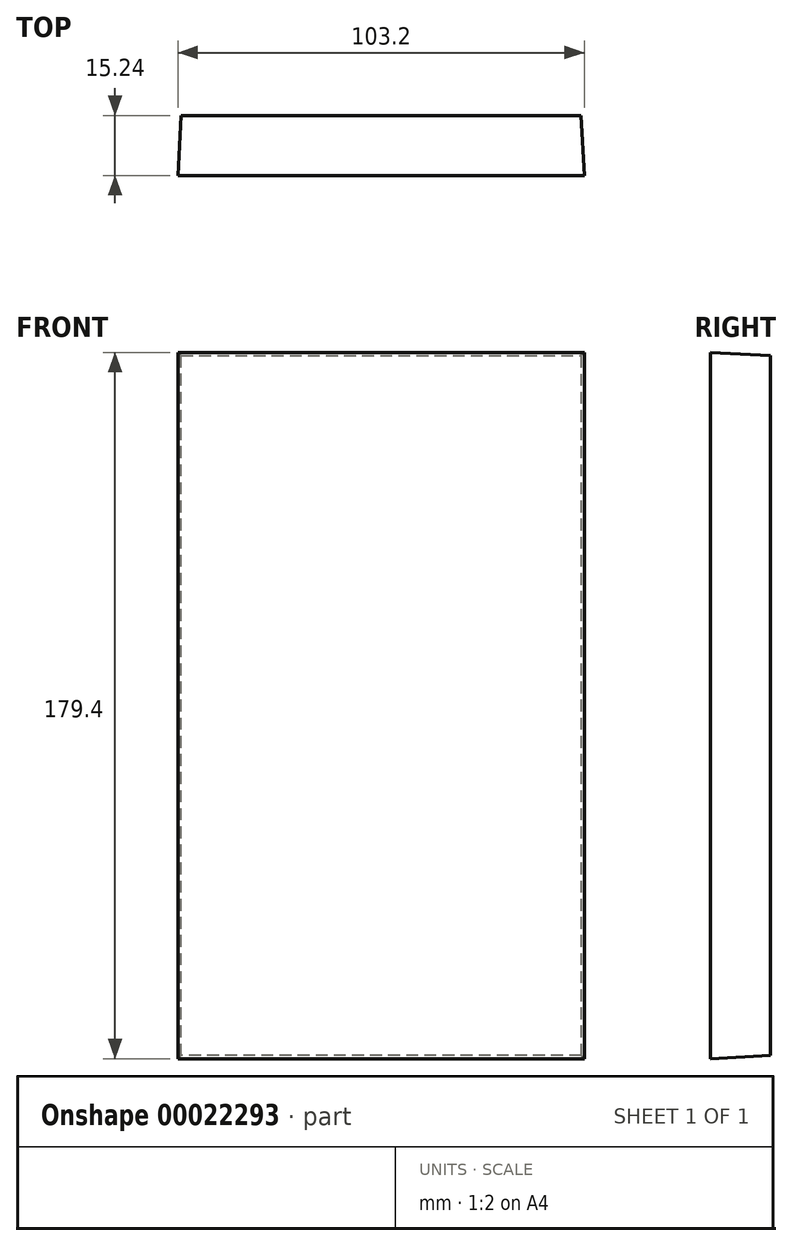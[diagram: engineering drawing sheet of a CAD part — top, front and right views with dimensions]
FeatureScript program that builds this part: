
annotation { "Feature Type Name" : "Feature", "Feature Type Description" : "" }
export const myFeature = defineFeature(function(context is Context, id is Id, definition is map)
    precondition{}
    {
        {
            var Q0;
            Q0=qCreatedBy(makeId("Front.planeOp"),FACE);
            var sketch = newSketch(context, id + "F0", { "sketchPlane" : qUnion([Q0])});
            skLineSegment(sketch, "E0.rect.bottom", {"start": v(50.8, -88.9) * mm, "end": v(-50.8, -88.9) * mm});
            skLineSegment(sketch, "E0.rect.top", {"start": v(50.8, 88.9) * mm, "end": v(-50.8, 88.9) * mm});
            skLineSegment(sketch, "E0.rect.left", {"start": v(50.8, -88.9) * mm, "end": v(50.8, 88.9) * mm});
            skLineSegment(sketch, "E0.rect.right", {"start": v(-50.8, -88.9) * mm, "end": v(-50.8, 88.9) * mm});
            skPoint(sketch, "E0.rect.middle", {"position": v(0, 0) * mm});
            skSolve(sketch);
        }
        {
            var Q0;
            Q0=makeQuery(id+"F0.imprint","IMPRINT",FACE,{"disambiguationData":[TD([[makeQuery(id+"F0.imprint","IMPRINT",EDGE,{"derivedFrom":sQuery(id+"F0.wireOp",EDGE,"E0.rect.bottom")}),-1.0]])]});
            extrude(context, id + "F1", {"entities" : qUnion([Q0]), "depth" : 15.24 * mm, "hasDraft" : true, "draftAngle" : 3 * degree});
        }
    });
